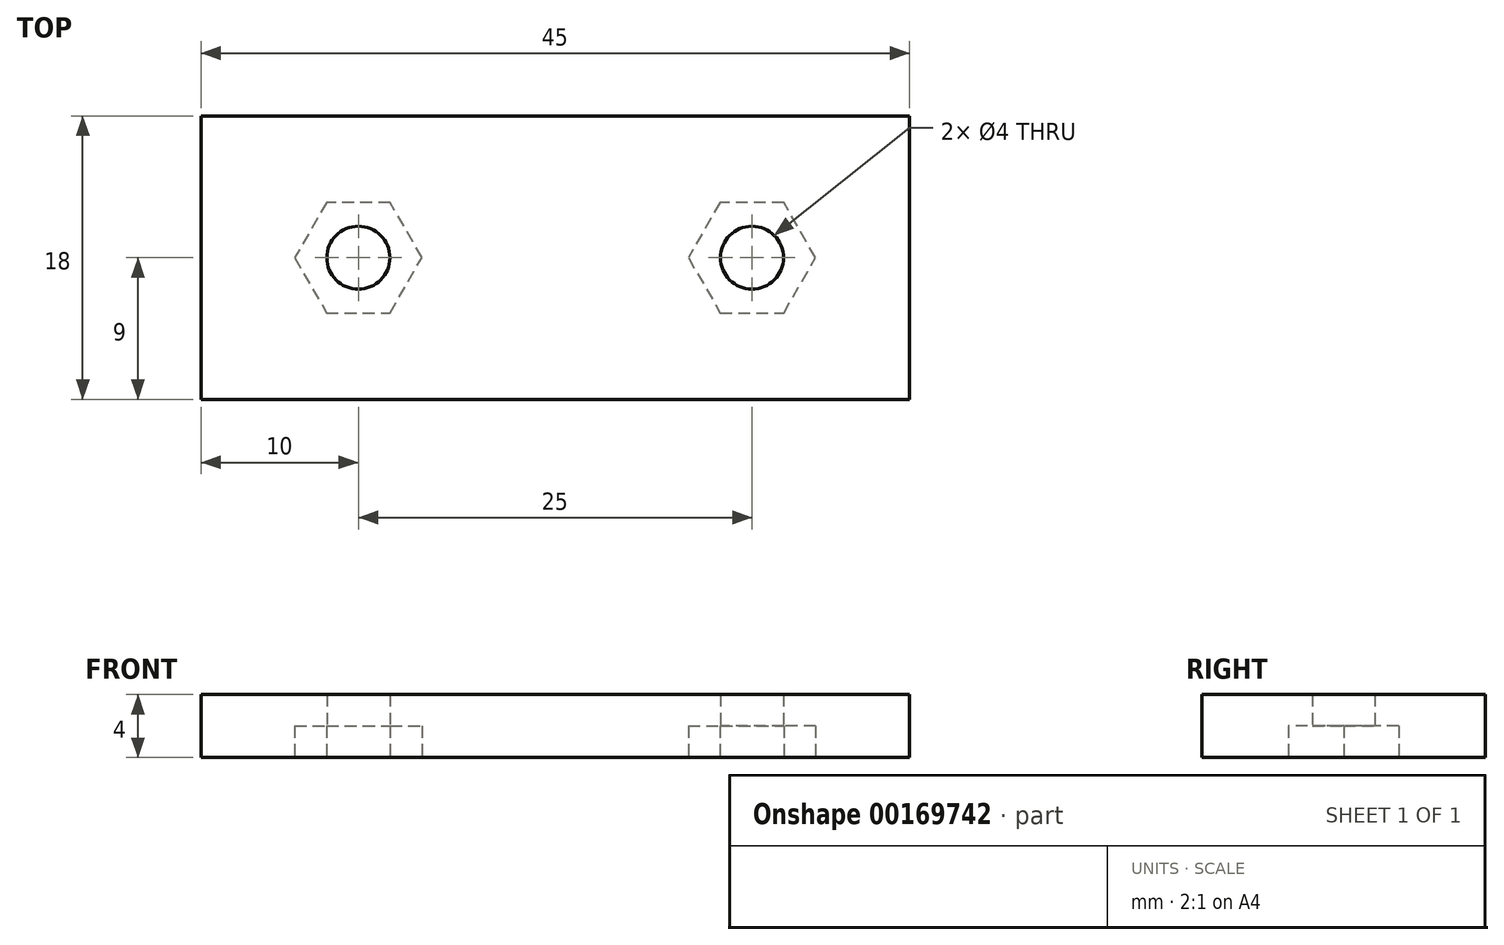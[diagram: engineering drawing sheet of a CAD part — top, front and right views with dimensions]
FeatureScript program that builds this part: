
annotation { "Feature Type Name" : "Feature", "Feature Type Description" : "" }
export const myFeature = defineFeature(function(context is Context, id is Id, definition is map)
    precondition{}
    {
        {
            var Q0;
            Q0=qCreatedBy(makeId("Top.planeOp"),FACE);
            var sketch = newSketch(context, id + "F0", { "sketchPlane" : qUnion([Q0])});
            skLineSegment(sketch, "E0.bottom", {"start": v(22.5, -9) * mm, "end": v(-22.5, -9) * mm});
            skLineSegment(sketch, "E0.top", {"start": v(22.5, 9) * mm, "end": v(-22.5, 9) * mm});
            skLineSegment(sketch, "E0.left", {"start": v(22.5, -9) * mm, "end": v(22.5, 9) * mm});
            skLineSegment(sketch, "E0.right", {"start": v(-22.5, -9) * mm, "end": v(-22.5, 9) * mm});
            skPoint(sketch, "E0.middle", {"position": v(0, 0) * mm});
            skLineSegment(sketch, "E1.0", {"start": v(-9, 2.02) * mm, "end": v(-9, -2.02) * mm});
            skLineSegment(sketch, "E1.1", {"start": v(-9, -2.02) * mm, "end": v(-12.5, -4.04) * mm});
            skLineSegment(sketch, "E1.2", {"start": v(-12.5, -4.04) * mm, "end": v(-16, -2.02) * mm});
            skLineSegment(sketch, "E1.3", {"start": v(-16, -2.02) * mm, "end": v(-16, 2.02) * mm});
            skLineSegment(sketch, "E1.4", {"start": v(-16, 2.02) * mm, "end": v(-12.5, 4.04) * mm});
            skLineSegment(sketch, "E1.5", {"start": v(-12.5, 4.04) * mm, "end": v(-9, 2.02) * mm});
            skPoint(sketch, "E1.0.midPoint", {"position": v(-9, 0) * mm});
            skLineSegment(sketch, "E2.0", {"start": v(16, 2.02) * mm, "end": v(16, -2.02) * mm});
            skLineSegment(sketch, "E2.1", {"start": v(16, -2.02) * mm, "end": v(12.5, -4.04) * mm});
            skLineSegment(sketch, "E2.2", {"start": v(12.5, -4.04) * mm, "end": v(9, -2.02) * mm});
            skLineSegment(sketch, "E2.3", {"start": v(9, -2.02) * mm, "end": v(9, 2.02) * mm});
            skLineSegment(sketch, "E2.4", {"start": v(9, 2.02) * mm, "end": v(12.5, 4.04) * mm});
            skLineSegment(sketch, "E2.5", {"start": v(12.5, 4.04) * mm, "end": v(16, 2.02) * mm});
            skPoint(sketch, "E2.0.midPoint", {"position": v(16, 0) * mm});
            skPoint(sketch, "E3", {"position": v(-12.5, 0) * mm});
            skPoint(sketch, "E3.positionSnap0", {"position": v(-16, 0) * mm});
            skPoint(sketch, "E4", {"position": v(12.5, 0) * mm});
            skPoint(sketch, "E4.positionSnap0", {"position": v(9, 0) * mm});
            skLineSegment(sketch, "E5", {"start": v(-22.5, 0) * mm, "end": v(22.5, 0) * mm, "construction": true});
            skCircle(sketch, "E6", {"center": v(-12.5, 0) * mm, "radius": 3.5 * mm, "construction": true});
            skSolve(sketch);
        }
        {
            var Q0;
            Q0=makeQuery(id+"F0.imprint","IMPRINT",FACE,{"disambiguationData":[TD([[makeQuery(id+"F0.imprint","IMPRINT",EDGE,{"derivedFrom":sQuery(id+"F0.wireOp",EDGE,"E0.bottom")}),-1.0]])]});
            var Q1;
            Q1=makeQuery(id+"F0.imprint","IMPRINT",FACE,{"disambiguationData":[TD([[makeQuery(id+"F0.imprint","IMPRINT",EDGE,{"derivedFrom":sQuery(id+"F0.wireOp",EDGE,"E1.0")}),-1.0]])]});
            var Q2;
            Q2=makeQuery(id+"F0.imprint","IMPRINT",FACE,{"disambiguationData":[TD([[makeQuery(id+"F0.imprint","IMPRINT",EDGE,{"derivedFrom":sQuery(id+"F0.wireOp",EDGE,"E2.0")}),-1.0]])]});
            extrude(context, id + "F1", {"entities" : qUnion([Q0, Q1, Q2]), "depth" : 4 * mm});
        }
        {
            var Q0;
            Q0=makeQuery(id+"F1.opExtrude","CAP_FACE",FACE,{"disambiguationData":[OSD([sQuery(id+"F0.wireOp",EDGE,"E0.bottom"),sQuery(id+"F0.wireOp",EDGE,"E0.top"),sQuery(id+"F0.wireOp",EDGE,"E0.left"),sQuery(id+"F0.wireOp",EDGE,"E0.right")])],"isStart":true});
            var sketch = newSketch(context, id + "F2", { "sketchPlane" : qUnion([Q0])});
            skLineSegment(sketch, "E7", {"start": v(-22.5, 0) * mm, "end": v(22.5, 0) * mm, "construction": true});
            skCircle(sketch, "E8", {"center": v(-12.5, 0) * mm, "radius": 3.5 * mm});
            skCircle(sketch, "E9", {"center": v(12.5, 0) * mm, "radius": 3.5 * mm});
            skCircle(sketch, "E10.cCircle", {"center": v(-12.5, 0) * mm, "radius": 3.5 * mm, "construction": true});
            skLineSegment(sketch, "E10.0", {"start": v(-14.52, 3.5) * mm, "end": v(-10.48, 3.5) * mm});
            skLineSegment(sketch, "E10.1", {"start": v(-10.48, 3.5) * mm, "end": v(-8.46, 0) * mm});
            skLineSegment(sketch, "E10.2", {"start": v(-8.46, 0) * mm, "end": v(-10.48, -3.5) * mm});
            skLineSegment(sketch, "E10.3", {"start": v(-10.48, -3.5) * mm, "end": v(-14.52, -3.5) * mm});
            skLineSegment(sketch, "E10.4", {"start": v(-14.52, -3.5) * mm, "end": v(-16.54, 0) * mm});
            skLineSegment(sketch, "E10.5", {"start": v(-16.54, 0) * mm, "end": v(-14.52, 3.5) * mm});
            skPoint(sketch, "E10.0.midPoint", {"position": v(-12.5, 3.5) * mm});
            skCircle(sketch, "E11.cCircle", {"center": v(12.5, 0) * mm, "radius": 3.5 * mm, "construction": true});
            skLineSegment(sketch, "E11.0", {"start": v(10.48, 3.5) * mm, "end": v(14.52, 3.5) * mm});
            skLineSegment(sketch, "E11.1", {"start": v(14.52, 3.5) * mm, "end": v(16.54, 0) * mm});
            skLineSegment(sketch, "E11.2", {"start": v(16.54, 0) * mm, "end": v(14.52, -3.5) * mm});
            skLineSegment(sketch, "E11.3", {"start": v(14.52, -3.5) * mm, "end": v(10.48, -3.5) * mm});
            skLineSegment(sketch, "E11.4", {"start": v(10.48, -3.5) * mm, "end": v(8.46, 0) * mm});
            skLineSegment(sketch, "E11.5", {"start": v(8.46, 0) * mm, "end": v(10.48, 3.5) * mm});
            skPoint(sketch, "E11.0.midPoint", {"position": v(12.5, 3.5) * mm});
            skSolve(sketch);
        }
        {
            var Q0;
            {var subQ0=sQuery(id+"F2.wireOp",EDGE,"E8");var subQ4=makeQuery(id+"F2.imprint","INTERSECT",VERTEX,{"derivedFrom":[subQ0,sQuery(id+"F2.wireOp",EDGE,"E10.0")]});Q0=makeQuery(id+"F2.imprint","IMPRINT",FACE,{"disambiguationData":[TD([[makeQuery(id+"F2.imprint","IMPRINT",EDGE,{"disambiguationData":[TD([[subQ4,1.0]])],"derivedFrom":subQ0}),1.0]])]});}
            var Q1;
            {var subQ0=sQuery(id+"F2.wireOp",EDGE,"E10.0");var subQ1=sQuery(id+"F2.wireOp",EDGE,"E8");var subQ2=makeQuery(id+"F2.imprint","INTERSECT",VERTEX,{"derivedFrom":[subQ1,subQ0]});Q1=makeQuery(id+"F2.imprint","IMPRINT",FACE,{"disambiguationData":[TD([[makeQuery(id+"F2.imprint","IMPRINT",EDGE,{"disambiguationData":[TD([[subQ2,-1.0]])],"derivedFrom":subQ1}),-1.0]])]});}
            var Q2;
            {var subQ0=sQuery(id+"F2.wireOp",EDGE,"E10.5");var subQ1=sQuery(id+"F2.wireOp",EDGE,"E8");var subQ2=makeQuery(id+"F2.imprint","INTERSECT",VERTEX,{"derivedFrom":[subQ1,subQ0]});Q2=makeQuery(id+"F2.imprint","IMPRINT",FACE,{"disambiguationData":[TD([[makeQuery(id+"F2.imprint","IMPRINT",EDGE,{"disambiguationData":[TD([[subQ2,-1.0]])],"derivedFrom":subQ1}),-1.0]])]});}
            var Q3;
            {var subQ0=sQuery(id+"F2.wireOp",EDGE,"E10.4");var subQ1=sQuery(id+"F2.wireOp",EDGE,"E8");var subQ2=makeQuery(id+"F2.imprint","INTERSECT",VERTEX,{"derivedFrom":[subQ1,subQ0]});Q3=makeQuery(id+"F2.imprint","IMPRINT",FACE,{"disambiguationData":[TD([[makeQuery(id+"F2.imprint","IMPRINT",EDGE,{"disambiguationData":[TD([[subQ2,-1.0]])],"derivedFrom":subQ1}),-1.0]])]});}
            var Q4;
            {var subQ0=sQuery(id+"F2.wireOp",EDGE,"E10.3");var subQ1=sQuery(id+"F2.wireOp",EDGE,"E8");var subQ2=makeQuery(id+"F2.imprint","INTERSECT",VERTEX,{"derivedFrom":[subQ1,subQ0]});Q4=makeQuery(id+"F2.imprint","IMPRINT",FACE,{"disambiguationData":[TD([[makeQuery(id+"F2.imprint","IMPRINT",EDGE,{"disambiguationData":[TD([[subQ2,-1.0]])],"derivedFrom":subQ1}),-1.0]])]});}
            var Q5;
            {var subQ0=sQuery(id+"F2.wireOp",EDGE,"E10.1");var subQ1=sQuery(id+"F2.wireOp",EDGE,"E8");var subQ2=makeQuery(id+"F2.imprint","INTERSECT",VERTEX,{"derivedFrom":[subQ1,subQ0]});Q5=makeQuery(id+"F2.imprint","IMPRINT",FACE,{"disambiguationData":[TD([[makeQuery(id+"F2.imprint","IMPRINT",EDGE,{"disambiguationData":[TD([[subQ2,1.0]])],"derivedFrom":subQ1}),-1.0]])]});}
            var Q6;
            {var subQ0=sQuery(id+"F2.wireOp",EDGE,"E10.0");var subQ1=sQuery(id+"F2.wireOp",EDGE,"E8");var subQ2=makeQuery(id+"F2.imprint","INTERSECT",VERTEX,{"derivedFrom":[subQ1,subQ0]});Q6=makeQuery(id+"F2.imprint","IMPRINT",FACE,{"disambiguationData":[TD([[makeQuery(id+"F2.imprint","IMPRINT",EDGE,{"disambiguationData":[TD([[subQ2,1.0]])],"derivedFrom":subQ1}),-1.0]])]});}
            var Q7;
            {var subQ0=sQuery(id+"F2.wireOp",EDGE,"E9");var subQ4=makeQuery(id+"F2.imprint","INTERSECT",VERTEX,{"derivedFrom":[subQ0,sQuery(id+"F2.wireOp",EDGE,"E11.0")]});Q7=makeQuery(id+"F2.imprint","IMPRINT",FACE,{"disambiguationData":[TD([[makeQuery(id+"F2.imprint","IMPRINT",EDGE,{"disambiguationData":[TD([[subQ4,1.0]])],"derivedFrom":subQ0}),1.0]])]});}
            var Q8;
            {var subQ0=sQuery(id+"F2.wireOp",EDGE,"E11.1");var subQ1=sQuery(id+"F2.wireOp",EDGE,"E9");var subQ2=makeQuery(id+"F2.imprint","INTERSECT",VERTEX,{"derivedFrom":[subQ1,subQ0]});Q8=makeQuery(id+"F2.imprint","IMPRINT",FACE,{"disambiguationData":[TD([[makeQuery(id+"F2.imprint","IMPRINT",EDGE,{"disambiguationData":[TD([[subQ2,1.0]])],"derivedFrom":subQ1}),-1.0]])]});}
            var Q9;
            {var subQ0=sQuery(id+"F2.wireOp",EDGE,"E11.3");var subQ1=sQuery(id+"F2.wireOp",EDGE,"E9");var subQ2=makeQuery(id+"F2.imprint","INTERSECT",VERTEX,{"derivedFrom":[subQ1,subQ0]});Q9=makeQuery(id+"F2.imprint","IMPRINT",FACE,{"disambiguationData":[TD([[makeQuery(id+"F2.imprint","IMPRINT",EDGE,{"disambiguationData":[TD([[subQ2,-1.0]])],"derivedFrom":subQ1}),-1.0]])]});}
            var Q10;
            {var subQ0=sQuery(id+"F2.wireOp",EDGE,"E11.4");var subQ1=sQuery(id+"F2.wireOp",EDGE,"E9");var subQ2=makeQuery(id+"F2.imprint","INTERSECT",VERTEX,{"derivedFrom":[subQ1,subQ0]});Q10=makeQuery(id+"F2.imprint","IMPRINT",FACE,{"disambiguationData":[TD([[makeQuery(id+"F2.imprint","IMPRINT",EDGE,{"disambiguationData":[TD([[subQ2,-1.0]])],"derivedFrom":subQ1}),-1.0]])]});}
            var Q11;
            {var subQ0=sQuery(id+"F2.wireOp",EDGE,"E11.5");var subQ1=sQuery(id+"F2.wireOp",EDGE,"E9");var subQ2=makeQuery(id+"F2.imprint","INTERSECT",VERTEX,{"derivedFrom":[subQ1,subQ0]});Q11=makeQuery(id+"F2.imprint","IMPRINT",FACE,{"disambiguationData":[TD([[makeQuery(id+"F2.imprint","IMPRINT",EDGE,{"disambiguationData":[TD([[subQ2,-1.0]])],"derivedFrom":subQ1}),-1.0]])]});}
            var Q12;
            {var subQ0=sQuery(id+"F2.wireOp",EDGE,"E11.0");var subQ1=sQuery(id+"F2.wireOp",EDGE,"E9");var subQ2=makeQuery(id+"F2.imprint","INTERSECT",VERTEX,{"derivedFrom":[subQ1,subQ0]});Q12=makeQuery(id+"F2.imprint","IMPRINT",FACE,{"disambiguationData":[TD([[makeQuery(id+"F2.imprint","IMPRINT",EDGE,{"disambiguationData":[TD([[subQ2,-1.0]])],"derivedFrom":subQ1}),-1.0]])]});}
            var Q13;
            {var subQ0=sQuery(id+"F2.wireOp",EDGE,"E11.0");var subQ1=sQuery(id+"F2.wireOp",EDGE,"E9");var subQ2=makeQuery(id+"F2.imprint","INTERSECT",VERTEX,{"derivedFrom":[subQ1,subQ0]});Q13=makeQuery(id+"F2.imprint","IMPRINT",FACE,{"disambiguationData":[TD([[makeQuery(id+"F2.imprint","IMPRINT",EDGE,{"disambiguationData":[TD([[subQ2,1.0]])],"derivedFrom":subQ1}),-1.0]])]});}
            extrude(context, id + "F3", {"entities" : qUnion([Q0, Q1, Q2, Q3, Q4, Q5, Q6, Q7, Q8, Q9, Q10, Q11, Q12, Q13]), "operationType" : NewBodyOperationType.REMOVE, "oppositeDirection" : true, "depth" : 2 * mm});
        }
        {
            var Q0;
            Q0=makeQuery(id+"F1.opExtrude","CAP_FACE",FACE,{"disambiguationData":[OSD([sQuery(id+"F0.wireOp",EDGE,"E0.bottom"),sQuery(id+"F0.wireOp",EDGE,"E0.top"),sQuery(id+"F0.wireOp",EDGE,"E0.left"),sQuery(id+"F0.wireOp",EDGE,"E0.right")])],"isStart":true});
            var sketch = newSketch(context, id + "F4", { "sketchPlane" : qUnion([Q0])});
            skCircle(sketch, "E12", {"center": v(-12.5, 0) * mm, "radius": 2 * mm});
            skPoint(sketch, "E12.centerSnap0", {"position": v(-12.5, 3.5) * mm});
            skCircle(sketch, "E13", {"center": v(12.5, 0) * mm, "radius": 2 * mm});
            skPoint(sketch, "E13.centerSnap0", {"position": v(12.5, 3.5) * mm});
            skSolve(sketch);
        }
        {
            var Q0;
            Q0=makeQuery(id+"F4.imprint","IMPRINT",FACE,{"disambiguationData":[TD([[makeQuery(id+"F4.imprint","IMPRINT",EDGE,{"derivedFrom":sQuery(id+"F4.wireOp",EDGE,"E12")}),1.0]])]});
            var Q1;
            Q1=makeQuery(id+"F4.imprint","IMPRINT",FACE,{"disambiguationData":[TD([[makeQuery(id+"F4.imprint","IMPRINT",EDGE,{"derivedFrom":sQuery(id+"F4.wireOp",EDGE,"E13")}),1.0]])]});
            extrude(context, id + "F5", {"entities" : qUnion([Q0, Q1]), "operationType" : NewBodyOperationType.REMOVE, "oppositeDirection" : true, "depth" : 25 * mm});
        }
    });
